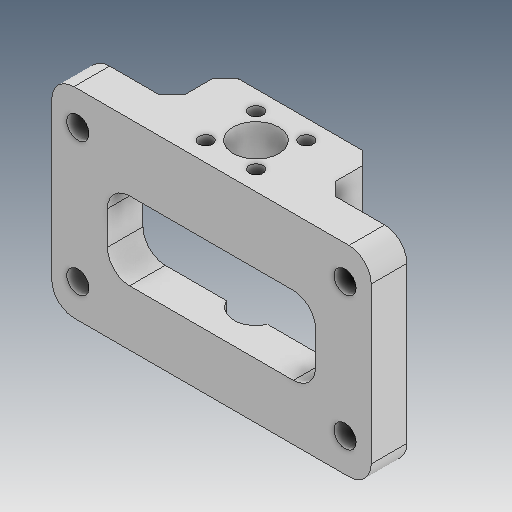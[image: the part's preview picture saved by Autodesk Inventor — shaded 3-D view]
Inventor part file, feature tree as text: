
AUTODESK INVENTOR PART (.ipt)
format: ipt  version: 2020 (Build 240168000, 168)  size: 154,112 bytes
history: native  units: mm
features: chamfer x1
ambient origin geometry x8: Origin, YZ Plane, XZ Plane, XY Plane, X Axis, Y Axis, Z Axis, Center Point
bodies: Solid1 (feature_tree)
feature tree (1):
  chamfer  "Chamfer3"  [1 undecoded]
note: 1 required parameter value undecoded (feature->parameter linkage not recoverable at this tier; creation-order binding heuristic only, values carry confidence <= 0.55)
